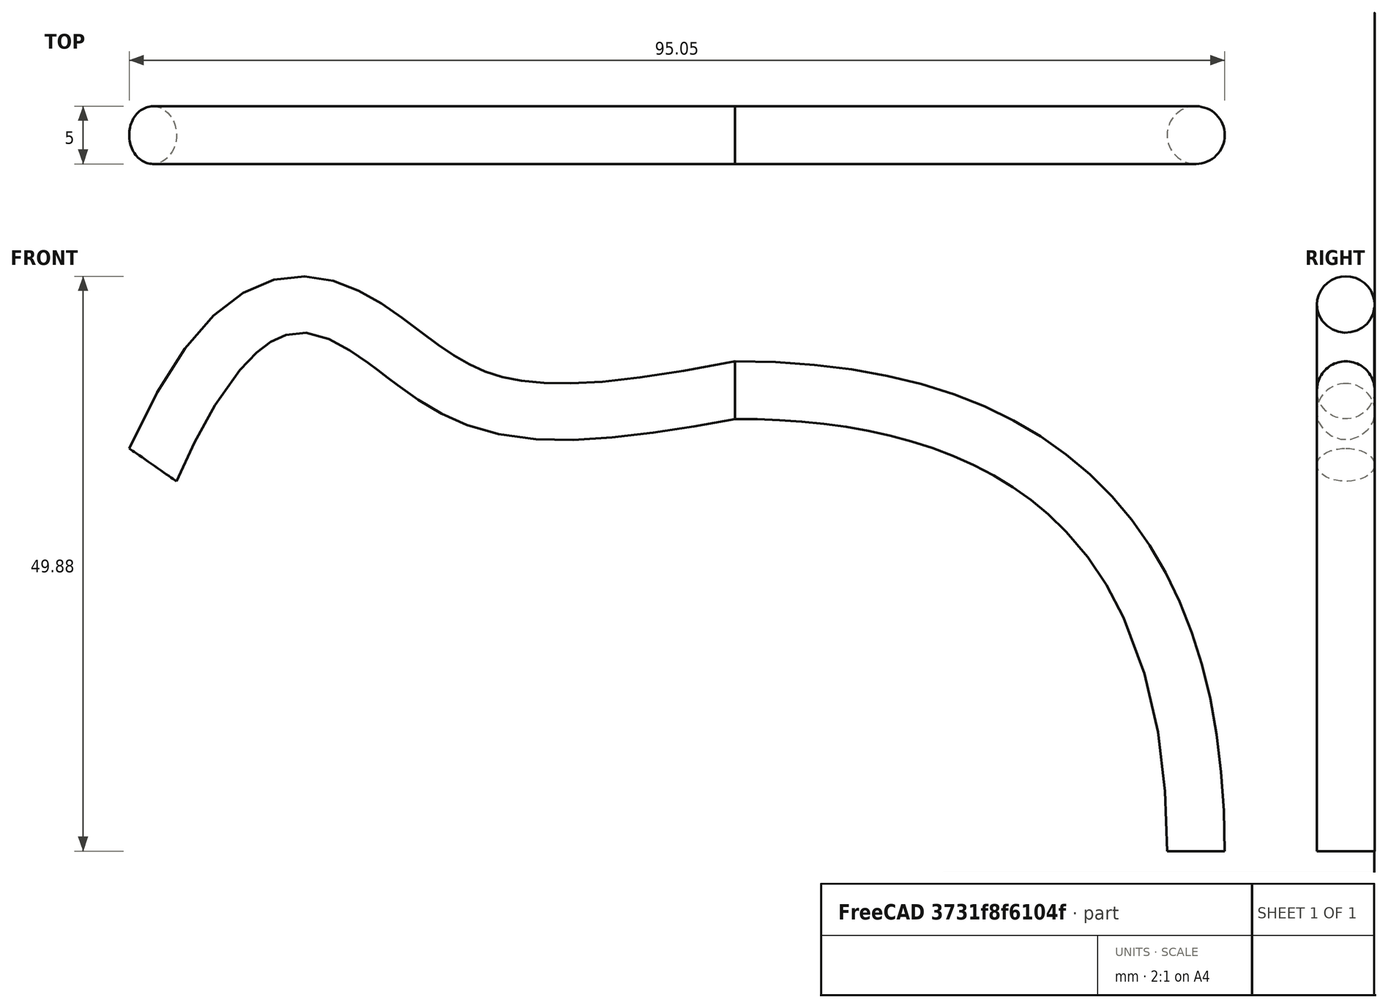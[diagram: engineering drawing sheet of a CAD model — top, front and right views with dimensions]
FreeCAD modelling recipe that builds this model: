
FCSTD DOCUMENT  (FreeCAD 1.0R39285 (Git))
Label: wire_6mm
License: All rights reserved
LicenseURL: https://en.wikipedia.org/wiki/All_rights_reserved
objects: Sketcher::SketchObject×2, PartDesign::AdditivePipe×1, PartDesign::Body×1
note: 8 computed .brp shape members not serialized (recipe doc carries the construction recipe); baked Part::Feature solids carry a one-line shape summary decoded from their .brp

FEATURE [Sketcher::SketchObject] Sketch
  ArcFitTolerance = 1e-06
  AttachmentSupport = -> [XZ_Plane]
  FullyConstrained = false
  MakeInternals = false
  MapMode = 5
  Placement = pos=(0,0,0) rot=(1,0,0;1.5708rad)
  sketch-geometry (15):
    g0: Circle [constr] CenterX=-40 CenterY=40 CenterZ=0 NormalX=0 NormalY=0 NormalZ=1 AngleXU=0 Radius=1
    g1: Circle [constr] CenterX=0 CenterY=40 CenterZ=0 NormalX=0 NormalY=0 NormalZ=1 AngleXU=0 Radius=1
    g2: Circle [constr] CenterX=0 CenterY=0 CenterZ=0 NormalX=0 NormalY=0 NormalZ=1 AngleXU=0 Radius=1
    g3: BSplineCurve PolesCount=3 KnotsCount=2 Degree=2 IsPeriodic=0
    g4: GeomPoint [constr] X=-40 Y=40 Z=0
    g5: GeomPoint [constr] X=0 Y=0 Z=0
    g6-g10: Circle [constr] x5 (B-spline internal-alignment scaffolding for g11; pole/knot coordinates omitted)
    g11: BSplineCurve PolesCount=5 KnotsCount=3 Degree=3 IsPeriodic=0
    g12: GeomPoint [constr] X=-40 Y=40 Z=0
    g13: GeomPoint [constr] X=-68.3423 Y=42.8049 Z=0
    g14: GeomPoint [constr] X=-90.4976 Y=33.5196 Z=0
  constraints (20):
    c: Weight(g0) = 1
    c: Equal(g0,g1)
    c: Equal(g0,g2)
    c: InternalAlignment(g0,g3)
    c: InternalAlignment(g1,g3)
    c: InternalAlignment(g2,g3)
    c: InternalAlignment(g4,g3)
    c: InternalAlignment(g5,g3)
    c: Coincident(g2,g-1)
    c: Vertical(g1,g3)
    c: Horizontal(g3,g1)
    c: DistanceY(g3,g1) = 40
    c: DistanceX(g3,g1) = 40
    c: Weight(g6) = 1
    c: Equal(g6, g7-g10) x4
    c: InternalAlignment(g6-g10 -> g11) x5
    c: InternalAlignment(g12,g11)
    c: InternalAlignment(g13,g11)
    c: InternalAlignment(g14,g11)
    c: Coincident(g6,g3)
FEATURE [Sketcher::SketchObject] Sketch001
  ArcFitTolerance = 1e-06
  AttachmentSupport = -> [XY_Plane]
  FullyConstrained = true
  MakeInternals = false
  MapMode = 5
  sketch-geometry (1):
    g0: Circle CenterX=0 CenterY=0 CenterZ=0 NormalX=0 NormalY=0 NormalZ=1 AngleXU=0 Radius=2.5
  constraints (2):
    c: Diameter(g0) = 5
    c: Coincident(g0,g-1)
FEATURE [PartDesign::AdditivePipe] AdditivePipe
  AuxilleryCurvelinear = true
  AuxillerySpineTangent = false
  Binormal = (0,0,0)
  Mode = 0
  Profile = -> Sketch001
  Refine = true
  Spine = -> Sketch
  SpineTangent = false
  Suppressed = false
  Transformation = 0
  Transition = 0
FEATURE [PartDesign::Body] Body
  AllowCompound = false
  Group = -> [Sketch,Sketch001,AdditivePipe]
  Origin = -> Origin
  Tip = -> AdditivePipe
